# Revit family: QF_COBRA MOFFAT_CW3H
name_source: partatom
category: Specialty Equipment
revit_build: Autodesk Revit 2016 (Build: 20150714_1515(x64)
units: mm (PartAtom-declared; Revit-internal decimal feet)

## family parameters
Always vertical = Yes
Cut with Voids When Loaded = No
Part Type = Normal
Room Calculation Point = No
Round Connector Dimension = Use Diameter
Shared = No
Work Plane-Based = No

## types (1)
- QF_COBRA MOFFAT_CW3H
    Cold Water Connection Height = 0 mm  [stored 0 ft]
    Cold Water Flow = 0 GPM
    Cold Water Maximum Pressure = 0.00 psi
    Cold Water Minimum Pressure = 0.00 psi
    Cold Water RI Height = 0 mm  [stored 0 ft]
    Cold Water Size = 2"
    Cold Water Temperature Recommended = 0 °F
    Depth = 800 mm
    Description = 3 HOLE GAS WATERLESS WOKS
    Foodservice Equipment Identifier = Yes
    Gas Connection Height = 0 mm  [stored 0 ft]
    Gas Input = 241693.0 Btu/h
    Gas KW = 0
    Gas RI Height = 0 mm  [stored 0 ft]
    Gas Size = 1"
    Height = 1280 mm
    Identify Quantity as Lot = Yes
    Indirect Waste Connection Height = 0 mm  [stored 0 ft]
    Indirect Waste Flow = 0 GPM
    Indirect Waste Size = 1"
    Length = 1800 mm  [stored 5.90551 ft]
    Manufacturer = COBRA MOFFAT
    Model = CW3H
    Waste Water Discharge Temperature = 0 °F
    Weight in Kilograms = 194

note: [stored X ft] marks values corroborated as IEEE doubles in the binary element streams (Revit-internal decimal feet)

## geometry (parser evidence)
native form markers: Sweep x2
no freeform markers — native parametric forms only
